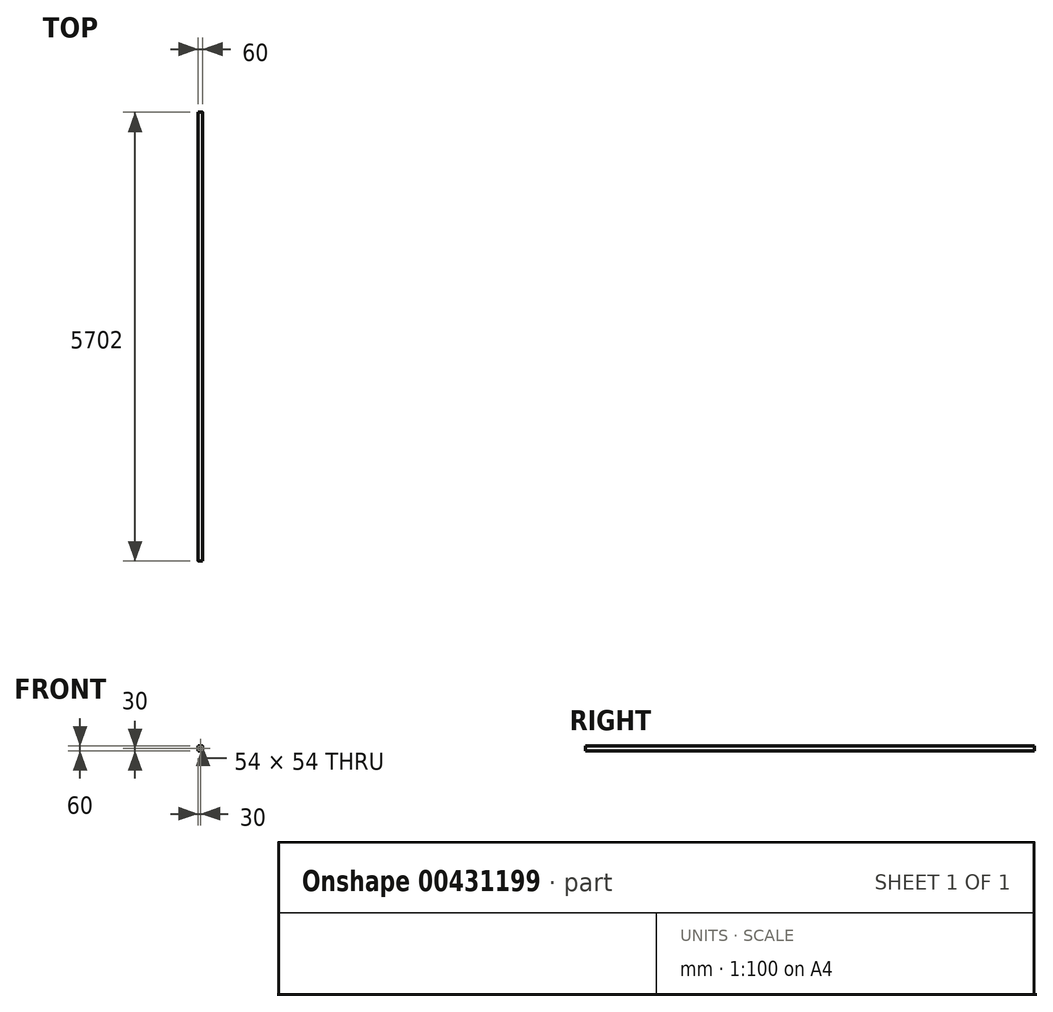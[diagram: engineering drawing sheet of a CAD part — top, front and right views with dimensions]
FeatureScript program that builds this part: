
annotation { "Feature Type Name" : "Feature", "Feature Type Description" : "" }
export const myFeature = defineFeature(function(context is Context, id is Id, definition is map)
    precondition{}
    {
        {
            var Q0;
            Q0=qCreatedBy(makeId("Front.planeOp"),FACE);
            var sketch = newSketch(context, id + "F0", { "sketchPlane" : qUnion([Q0])});
            skLineSegment(sketch, "E0.bottom", {"start": v(27, -30) * mm, "end": v(-27, -30) * mm});
            skLineSegment(sketch, "E0.top", {"start": v(27, 30) * mm, "end": v(-27, 30) * mm});
            skLineSegment(sketch, "E0.left", {"start": v(30, -27) * mm, "end": v(30, 27) * mm});
            skLineSegment(sketch, "E0.right", {"start": v(-30, -27) * mm, "end": v(-30, 27) * mm});
            skPoint(sketch, "E0.middle", {"position": v(0, 0) * mm});
            skLineSegment(sketch, "E1.bottom", {"start": v(27, -27) * mm, "end": v(-27, -27) * mm});
            skLineSegment(sketch, "E1.top", {"start": v(27, 27) * mm, "end": v(-27, 27) * mm});
            skLineSegment(sketch, "E1.left", {"start": v(27, -27) * mm, "end": v(27, 27) * mm});
            skLineSegment(sketch, "E1.right", {"start": v(-27, -27) * mm, "end": v(-27, 27) * mm});
            skPoint(sketch, "E2.visualSharp", {"position": v(-30, 30) * mm});
            skArc(sketch, "E2.filletArc", {"start": v(-27, 30) * mm, "mid": v(-29.12, 29.12) * mm, "end": v(-30, 27) * mm});
            skPoint(sketch, "E3.visualSharp", {"position": v(30, 30) * mm});
            skArc(sketch, "E3.filletArc", {"start": v(30, 27) * mm, "mid": v(29.12, 29.12) * mm, "end": v(27, 30) * mm});
            skPoint(sketch, "E4.visualSharp", {"position": v(30, -30) * mm});
            skArc(sketch, "E4.filletArc", {"start": v(27, -30) * mm, "mid": v(29.12, -29.12) * mm, "end": v(30, -27) * mm});
            skPoint(sketch, "E5.visualSharp", {"position": v(-30, -30) * mm});
            skArc(sketch, "E5.filletArc", {"start": v(-30, -27) * mm, "mid": v(-29.12, -29.12) * mm, "end": v(-27, -30) * mm});
            skSolve(sketch);
        }
        {
            var Q0;
            Q0=makeQuery(id+"F0.imprint","IMPRINT",FACE,{"disambiguationData":[TD([[makeQuery(id+"F0.imprint","IMPRINT",EDGE,{"derivedFrom":sQuery(id+"F0.wireOp",EDGE,"E0.bottom")}),-1.0]])]});
            extrude(context, id + "F1", {"entities" : qUnion([Q0]), "depth" : 5702 * mm});
        }
    });
